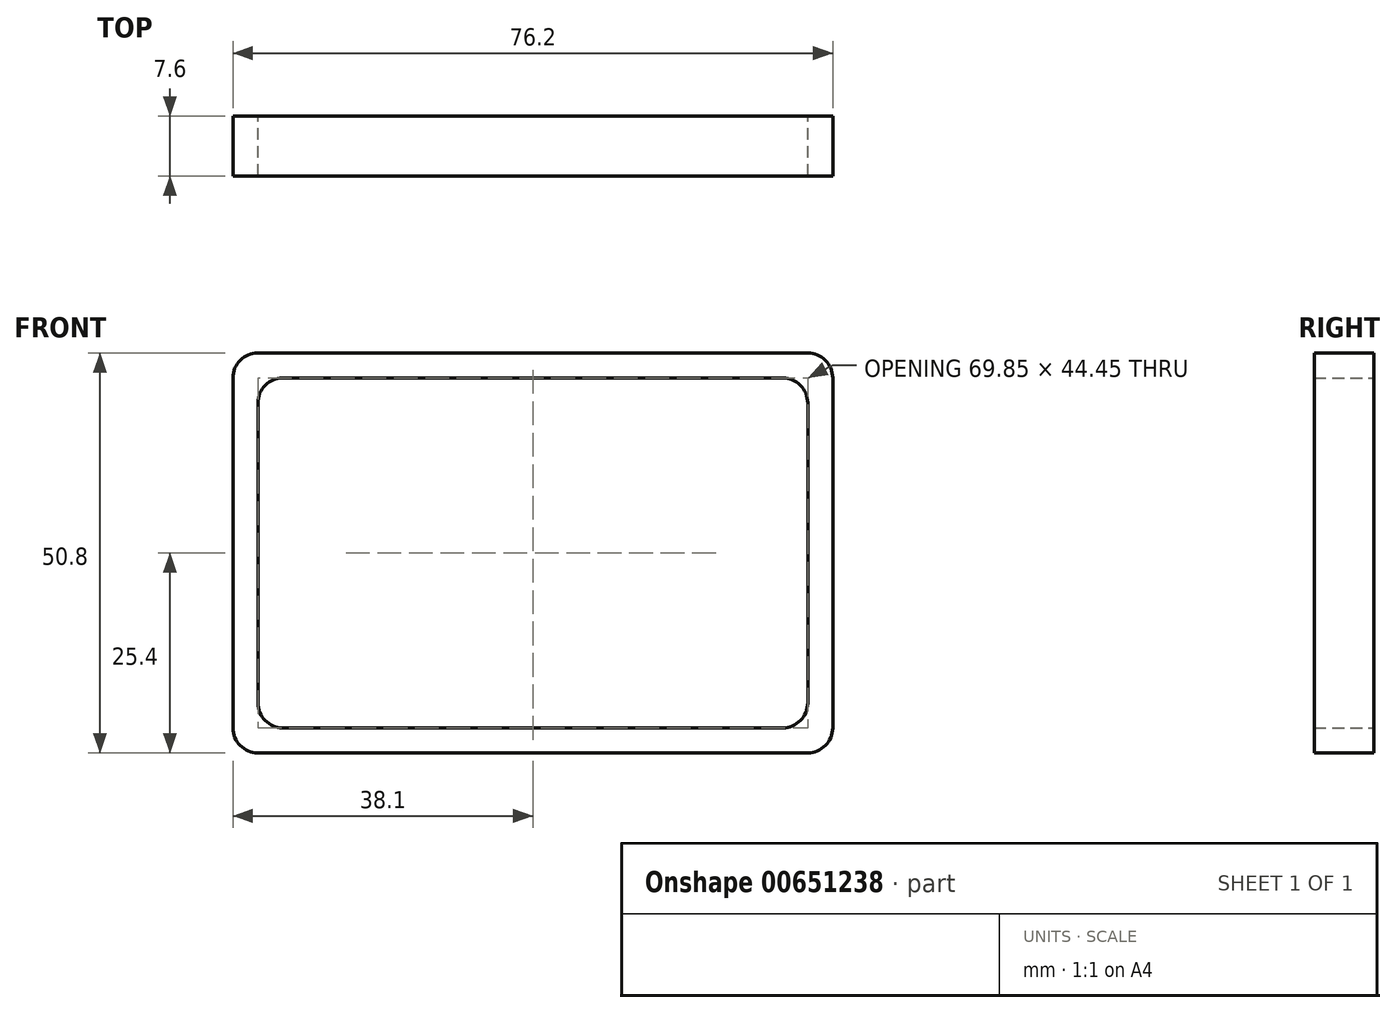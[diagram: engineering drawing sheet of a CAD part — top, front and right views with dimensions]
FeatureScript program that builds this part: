
annotation { "Feature Type Name" : "Feature", "Feature Type Description" : "" }
export const myFeature = defineFeature(function(context is Context, id is Id, definition is map)
    precondition{}
    {
        {
            var Q0;
            Q0=qCreatedBy(makeId("Front.planeOp"),FACE);
            var sketch = newSketch(context, id + "F0", { "sketchPlane" : qUnion([Q0])});
            skLineSegment(sketch, "E0.bottom", {"start": v(38.1, -25.4) * mm, "end": v(-38.1, -25.4) * mm});
            skLineSegment(sketch, "E0.top", {"start": v(38.1, 25.4) * mm, "end": v(-38.1, 25.4) * mm});
            skLineSegment(sketch, "E0.left", {"start": v(38.1, -25.4) * mm, "end": v(38.1, 25.4) * mm});
            skLineSegment(sketch, "E0.right", {"start": v(-38.1, -25.4) * mm, "end": v(-38.1, 25.4) * mm});
            skPoint(sketch, "E0.middle", {"position": v(0, 0) * mm});
            skLineSegment(sketch, "E1.bottom", {"start": v(34.93, -22.22) * mm, "end": v(-34.93, -22.23) * mm});
            skLineSegment(sketch, "E1.top", {"start": v(34.93, 22.23) * mm, "end": v(-34.93, 22.22) * mm});
            skLineSegment(sketch, "E1.left", {"start": v(34.93, -22.22) * mm, "end": v(34.93, 22.23) * mm});
            skLineSegment(sketch, "E1.right", {"start": v(-34.93, -22.23) * mm, "end": v(-34.93, 22.22) * mm});
            skSolve(sketch);
        }
        {
            assignVariable(context, id + "F1", {"name" : "Length", "anyValue" : 7.6});
        }
        {
            var Q0;
            Q0=makeQuery(id+"F0.imprint","IMPRINT",FACE,{"disambiguationData":[TD([[makeQuery(id+"F0.imprint","IMPRINT",EDGE,{"derivedFrom":sQuery(id+"F0.wireOp",EDGE,"E0.bottom")}),-1.0]])]});
            extrude(context, id + "F2", {"entities" : qUnion([Q0]), "depth" : (getVariable(context, 'Length')) * mm, "offsetDistance" : 25.4 * mm});
        }
        {
            var Q0;
            Q0=makeQuery(id+"F2.opExtrude","SWEPT_EDGE",EDGE,{"disambiguationData":[OSD([sQuery(id+"F0.wireOp",EDGE,"E0.bottom"),sQuery(id+"F0.wireOp",EDGE,"E0.right")])]});
            var Q1;
            Q1=makeQuery(id+"F2.opExtrude","SWEPT_EDGE",EDGE,{"disambiguationData":[OSD([sQuery(id+"F0.wireOp",EDGE,"E0.top"),sQuery(id+"F0.wireOp",EDGE,"E0.right")])]});
            var Q2;
            Q2=makeQuery(id+"F2.opExtrude","SWEPT_EDGE",EDGE,{"disambiguationData":[OSD([sQuery(id+"F0.wireOp",EDGE,"E0.bottom"),sQuery(id+"F0.wireOp",EDGE,"E0.left")])]});
            var Q3;
            Q3=makeQuery(id+"F2.opExtrude","SWEPT_EDGE",EDGE,{"disambiguationData":[OSD([sQuery(id+"F0.wireOp",EDGE,"E0.top"),sQuery(id+"F0.wireOp",EDGE,"E0.left")])]});
            var Q4;
            Q4=makeQuery(id+"F2.opExtrude","SWEPT_EDGE",EDGE,{"disambiguationData":[OSD([sQuery(id+"F0.wireOp",EDGE,"E1.bottom"),sQuery(id+"F0.wireOp",EDGE,"E1.right")])]});
            var Q5;
            Q5=makeQuery(id+"F2.opExtrude","SWEPT_EDGE",EDGE,{"disambiguationData":[OSD([sQuery(id+"F0.wireOp",EDGE,"E1.top"),sQuery(id+"F0.wireOp",EDGE,"E1.right")])]});
            var Q6;
            Q6=makeQuery(id+"F2.opExtrude","SWEPT_EDGE",EDGE,{"disambiguationData":[OSD([sQuery(id+"F0.wireOp",EDGE,"E1.top"),sQuery(id+"F0.wireOp",EDGE,"E1.left")])]});
            var Q7;
            Q7=makeQuery(id+"F2.opExtrude","SWEPT_EDGE",EDGE,{"disambiguationData":[OSD([sQuery(id+"F0.wireOp",EDGE,"E1.bottom"),sQuery(id+"F0.wireOp",EDGE,"E1.left")])]});
            fillet(context, id + "F3", {"entities" : qUnion([Q0, Q1, Q2, Q3, Q4, Q5, Q6, Q7]), "radius" : 3.17 * mm, "tangentPropagation" : true, "allowEdgeOverflow" : false});
        }
        {
            var Q0;
            Q0=makeQuery(id+"F2.opExtrude","SWEPT_FACE",FACE,{"disambiguationData":[OSD([sQuery(id+"F0.wireOp",EDGE,"E0.bottom")])]});
            var sketch = newSketch(context, id + "F4", { "sketchPlane" : qUnion([Q0])});
            skLineSegment(sketch, "E2", {"start": v(0, 0) * mm, "end": v(0, 96.52) * mm});
            skPoint(sketch, "E3.middle", {"position": v(0, 96.52) * mm});
            skCircle(sketch, "E4", {"center": v(12.7, 58.42) * mm, "radius": 3 * mm});
            skCircle(sketch, "E5", {"center": v(-12.7, 58.42) * mm, "radius": 3 * mm});
            skCircle(sketch, "E6", {"center": v(-12.7, 134.62) * mm, "radius": 3 * mm});
            skCircle(sketch, "E7", {"center": v(12.7, 134.62) * mm, "radius": 3 * mm});
            skSolve(sketch);
        }
        {
            var Q0;
            Q0=makeQuery(id+"F4.imprint","IMPRINT",FACE,{"disambiguationData":[TD([[makeQuery(id+"F4.imprint","IMPRINT",EDGE,{"derivedFrom":sQuery(id+"F4.wireOp",EDGE,"E5")}),1.0]])]});
            var Q1;
            Q1=makeQuery(id+"F4.imprint","IMPRINT",FACE,{"disambiguationData":[TD([[makeQuery(id+"F4.imprint","IMPRINT",EDGE,{"derivedFrom":sQuery(id+"F4.wireOp",EDGE,"E4")}),1.0]])]});
            var Q2;
            Q2=makeQuery(id+"F4.imprint","IMPRINT",FACE,{"disambiguationData":[TD([[makeQuery(id+"F4.imprint","IMPRINT",EDGE,{"derivedFrom":sQuery(id+"F4.wireOp",EDGE,"E7")}),1.0]])]});
            var Q3;
            Q3=makeQuery(id+"F4.imprint","IMPRINT",FACE,{"disambiguationData":[TD([[makeQuery(id+"F4.imprint","IMPRINT",EDGE,{"derivedFrom":sQuery(id+"F4.wireOp",EDGE,"E6")}),1.0]])]});
            extrude(context, id + "F5", {"entities" : qUnion([Q0, Q1, Q2, Q3]), "operationType" : NewBodyOperationType.REMOVE, "oppositeDirection" : true, "depth" : 25.4 * mm, "offsetDistance" : 25.4 * mm});
        }
        {
            var Q0;
            Q0=makeQuery(id+"F2.opExtrude","SWEPT_FACE",FACE,{"disambiguationData":[OSD([sQuery(id+"F0.wireOp",EDGE,"E0.top")])]});
            var sketch = newSketch(context, id + "F6", { "sketchPlane" : qUnion([Q0])});
            skLineSegment(sketch, "E8", {"start": v(0, 0) * mm, "end": v(0, -96.52) * mm});
            skLineSegment(sketch, "E9.bottom", {"start": v(-38.1, -160.02) * mm, "end": v(38.1, -160.02) * mm});
            skLineSegment(sketch, "E9.top", {"start": v(-38.1, -33.02) * mm, "end": v(38.1, -33.02) * mm});
            skLineSegment(sketch, "E9.left", {"start": v(-38.1, -160.02) * mm, "end": v(-38.1, -33.02) * mm});
            skLineSegment(sketch, "E9.right", {"start": v(38.1, -160.02) * mm, "end": v(38.1, -33.02) * mm});
            skPoint(sketch, "E9.middle", {"position": v(0, -96.52) * mm});
            skSolve(sketch);
        }
        {
            var Q0;
            {var subQ5=sQuery(id+"F6.wireOp",EDGE,"E9.top");var subQ9=makeQuery(id+"F6.imprint","INTERSECT",VERTEX,{"derivedFrom":[sQuery(id+"F6.wireOp",EDGE,"E8"),subQ5]});Q0=makeQuery(id+"F6.imprint","IMPRINT",FACE,{"disambiguationData":[TD([[makeQuery(id+"F6.imprint","IMPRINT",EDGE,{"disambiguationData":[TD([[subQ9,1.0]])],"derivedFrom":subQ5}),-1.0]])]});}
            extrude(context, id + "F7", {"entities" : qUnion([Q0]), "operationType" : NewBodyOperationType.REMOVE, "oppositeDirection" : true, "depth" : 25.4 * mm, "offsetDistance" : 25.4 * mm});
        }
    });
